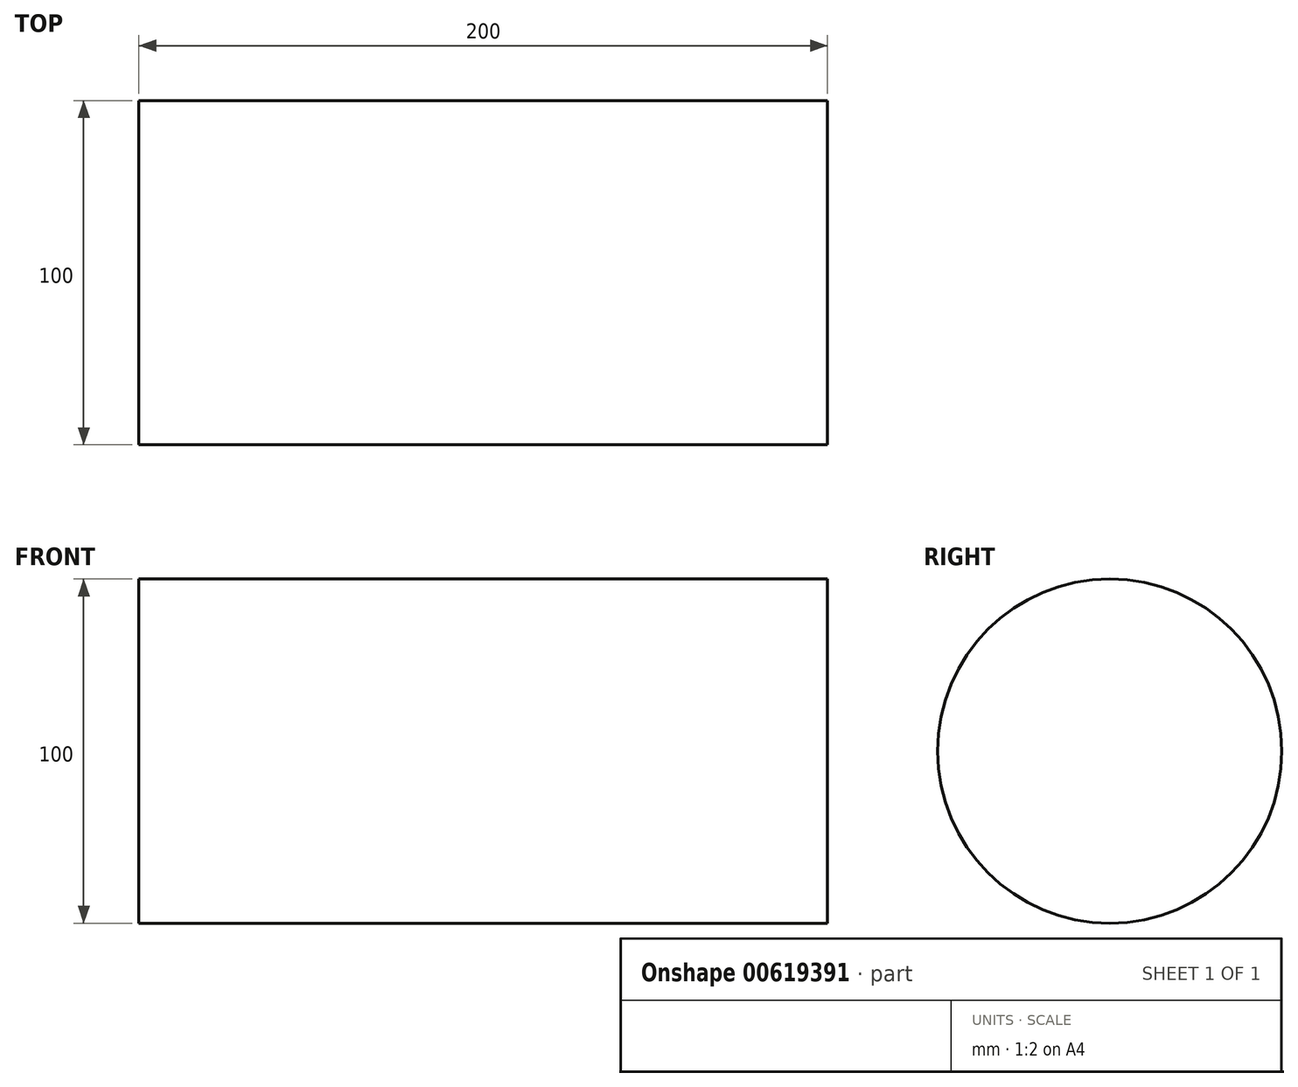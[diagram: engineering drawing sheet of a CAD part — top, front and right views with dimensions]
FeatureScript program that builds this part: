
annotation { "Feature Type Name" : "Feature", "Feature Type Description" : "" }
export const myFeature = defineFeature(function(context is Context, id is Id, definition is map)
    precondition{}
    {
        {
            var Q0;
            Q0=qCreatedBy(makeId("Right.planeOp"),FACE);
            var sketch = newSketch(context, id + "F0", { "sketchPlane" : qUnion([Q0])});
            skCircle(sketch, "E0", {"center": v(0, 0) * mm, "radius": 50 * mm});
            skSolve(sketch);
        }
        {
            var Q0;
            Q0=makeQuery(id+"F0.imprint","IMPRINT",FACE,{"disambiguationData":[TD([[makeQuery(id+"F0.imprint","IMPRINT",EDGE,{"derivedFrom":sQuery(id+"F0.wireOp",EDGE,"E0")}),1.0]])]});
            extrude(context, id + "F1", {"entities" : qUnion([Q0]), "depth" : 200 * mm, "offsetDistance" : 25.4 * mm});
        }
    });
